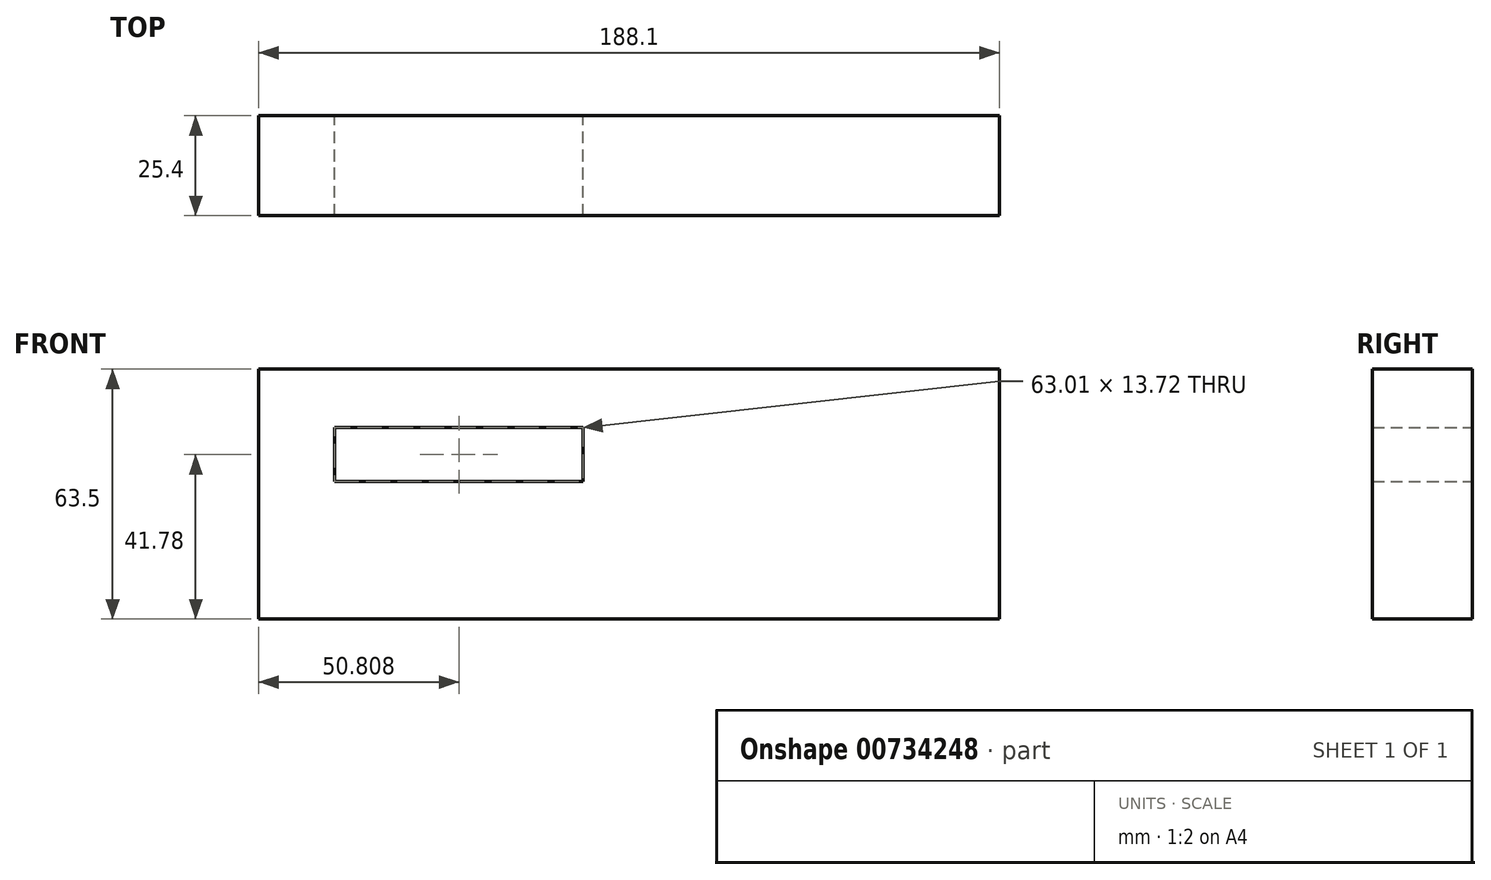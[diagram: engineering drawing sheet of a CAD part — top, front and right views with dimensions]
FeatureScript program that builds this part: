
annotation { "Feature Type Name" : "Feature", "Feature Type Description" : "" }
export const myFeature = defineFeature(function(context is Context, id is Id, definition is map)
    precondition{}
    {
        {
            var Q0;
            Q0=qCreatedBy(makeId("Front.planeOp"),FACE);
            var sketch = newSketch(context, id + "F0", { "sketchPlane" : qUnion([Q0])});
            skLineSegment(sketch, "E0", {"start": v(-94.4, 0) * mm, "end": v(-94.4, 63.5) * mm});
            skLineSegment(sketch, "E1", {"start": v(-94.4, 63.5) * mm, "end": v(-11.85, 63.5) * mm});
            skLineSegment(sketch, "E2", {"start": v(-11.85, 63.5) * mm, "end": v(93.7, 63.5) * mm});
            skLineSegment(sketch, "E3", {"start": v(93.7, 63.5) * mm, "end": v(93.7, 0) * mm});
            skLineSegment(sketch, "E4", {"start": v(93.7, 0) * mm, "end": v(-94.4, 0) * mm});
            skLineSegment(sketch, "E5.bottom", {"start": v(-75.1, 34.92) * mm, "end": v(-12.09, 34.92) * mm});
            skLineSegment(sketch, "E5.top", {"start": v(-75.1, 48.64) * mm, "end": v(-12.09, 48.64) * mm});
            skLineSegment(sketch, "E5.left", {"start": v(-75.1, 34.92) * mm, "end": v(-75.1, 48.64) * mm});
            skLineSegment(sketch, "E5.right", {"start": v(-12.09, 34.92) * mm, "end": v(-12.09, 48.64) * mm});
            skLineSegment(sketch, "E6", {"start": v(-6.75, 48.64) * mm, "end": v(79.63, 48.64) * mm});
            skLineSegment(sketch, "E7", {"start": v(-6.75, 29.59) * mm, "end": v(79.63, 29.59) * mm});
            skLineSegment(sketch, "E8", {"start": v(-56.05, 29.84) * mm, "end": v(-56.05, -11.3) * mm});
            skLineSegment(sketch, "E9", {"start": v(-75.1, 28.83) * mm, "end": v(-75.1, -12.58) * mm});
            skLineSegment(sketch, "E10", {"start": v(-11.85, 63.5) * mm, "end": v(-11.85, 0) * mm});
            skSolve(sketch);
        }
        {
            var Q0;
            {var subQ1=sQuery(id+"F0.wireOp",EDGE,"E0");Q0=makeQuery(id+"F0.imprint","IMPRINT",FACE,{"disambiguationData":[TD([[makeQuery(id+"F0.imprint","IMPRINT",EDGE,{"derivedFrom":subQ1}),-1.0]])]});}
            var Q1;
            Q1=makeQuery(id+"F0.imprint","IMPRINT",FACE,{"disambiguationData":[TD([[makeQuery(id+"F0.imprint","IMPRINT",EDGE,{"derivedFrom":sQuery(id+"F0.wireOp",EDGE,"E2")}),-1.0]])]});
            extrude(context, id + "F1", {"entities" : qUnion([Q0, Q1]), "depth" : 25.4 * mm, "offsetDistance" : 25.4 * mm});
        }
    });
